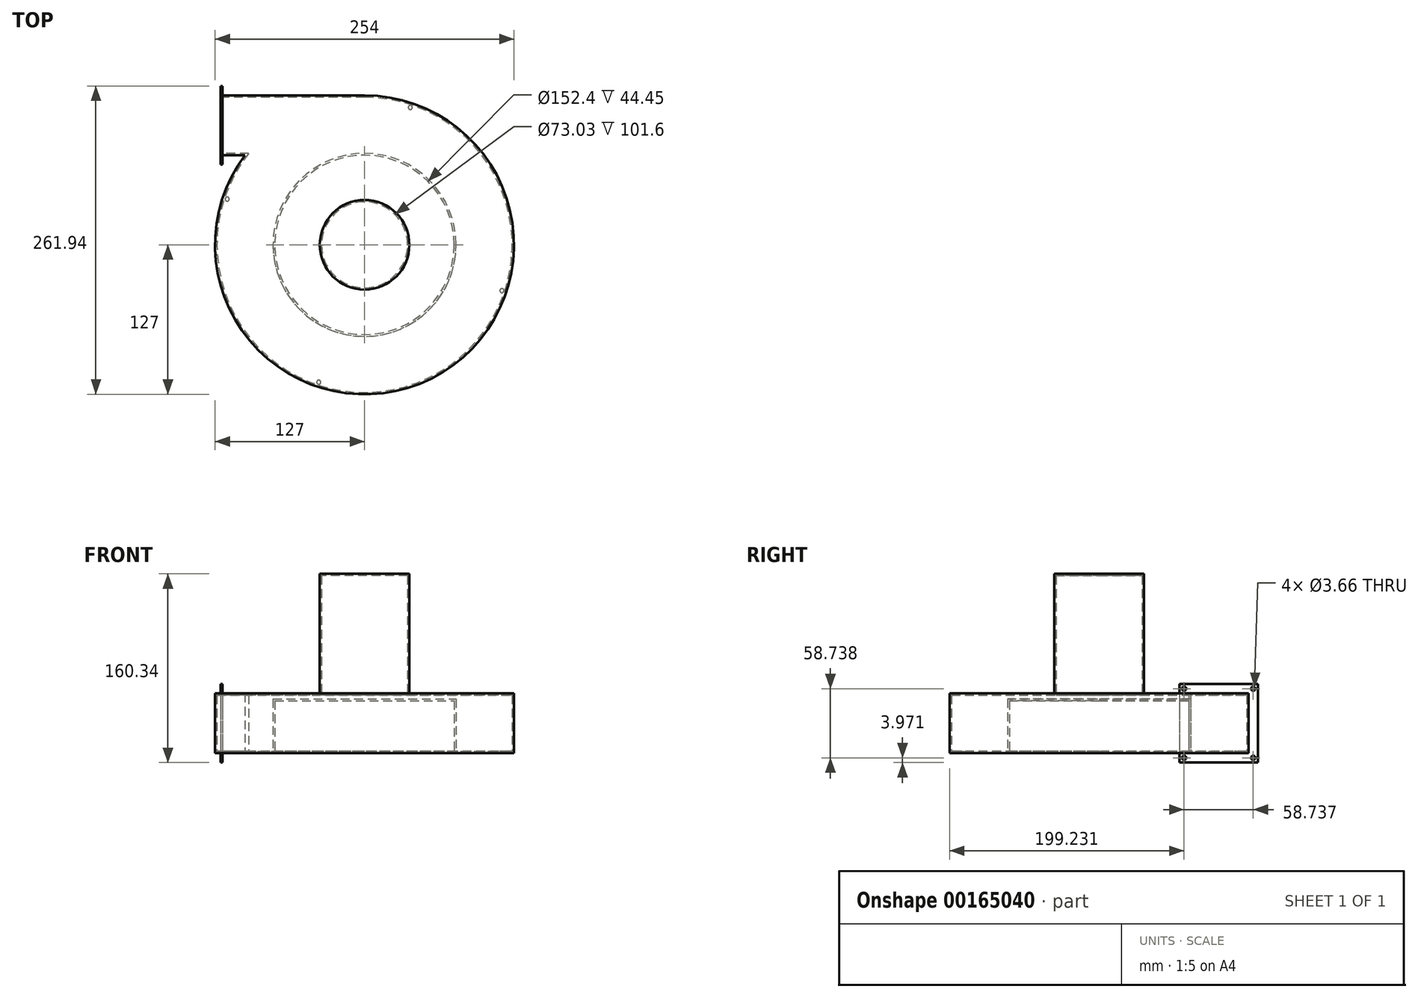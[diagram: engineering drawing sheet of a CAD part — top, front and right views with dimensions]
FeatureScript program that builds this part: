
annotation { "Feature Type Name" : "Feature", "Feature Type Description" : "" }
export const myFeature = defineFeature(function(context is Context, id is Id, definition is map)
    precondition{}
    {
        {
            var Q0;
            Q0=qCreatedBy(makeId("Top.planeOp"),FACE);
            var sketch = newSketch(context, id + "F0", { "sketchPlane" : qUnion([Q0])});
            skLineSegment(sketch, "E0.bottom", {"start": v(-101.6, 76.2) * mm, "end": v(-120.65, 76.2) * mm});
            skLineSegment(sketch, "E0.top", {"start": v(0, 127) * mm, "end": v(-120.65, 127) * mm});
            skLineSegment(sketch, "E1.top", {"start": v(-120.65, 68.26) * mm, "end": v(-122.24, 68.26) * mm});
            skLineSegment(sketch, "E1.left", {"start": v(-120.65, 76.2) * mm, "end": v(-120.65, 68.26) * mm});
            skLineSegment(sketch, "E2.top", {"start": v(-120.65, 134.94) * mm, "end": v(-122.24, 134.94) * mm});
            skLineSegment(sketch, "E2.left", {"start": v(-120.65, 127) * mm, "end": v(-120.65, 134.94) * mm});
            skLineSegment(sketch, "E3", {"start": v(-122.24, 134.94) * mm, "end": v(-122.24, 68.26) * mm});
            skLineSegment(sketch, "E4", {"start": v(-120.65, 76.2) * mm, "end": v(-120.65, 127) * mm, "construction": true});
            skArc(sketch, "E5", {"start": v(-101.6, 76.2) * mm, "mid": v(56.8, -113.6) * mm, "end": v(0, 127) * mm});
            skSolve(sketch);
        }
        {
            var Q0;
            Q0=makeQuery(id+"F0.imprint","IMPRINT",FACE,{"disambiguationData":[TD([[makeQuery(id+"F0.imprint","IMPRINT",EDGE,{"derivedFrom":sQuery(id+"F0.wireOp",EDGE,"E0.bottom")}),-1.0]])]});
            extrude(context, id + "F1", {"entities" : qUnion([Q0]), "depth" : 50.8 * mm});
        }
        {
            var Q0;
            Q0=makeQuery(id+"F1.opExtrude","CAP_FACE",FACE,{"disambiguationData":[OSD([sQuery(id+"F0.wireOp",EDGE,"E0.bottom"),sQuery(id+"F0.wireOp",EDGE,"E0.top"),sQuery(id+"F0.wireOp",EDGE,"E1.top"),sQuery(id+"F0.wireOp",EDGE,"E1.left"),sQuery(id+"F0.wireOp",EDGE,"E2.top"),sQuery(id+"F0.wireOp",EDGE,"E2.left"),sQuery(id+"F0.wireOp",EDGE,"E3"),sQuery(id+"F0.wireOp",EDGE,"E5")])],"isStart":true});
            var sketch = newSketch(context, id + "F2", { "sketchPlane" : qUnion([Q0])});
            skCircle(sketch, "E6", {"center": v(0, 0) * mm, "radius": 76.2 * mm});
            skSolve(sketch);
        }
        {
            var Q0;
            Q0=qSketchRegion(id+"F2",true);
            extrude(context, id + "F3", {"entities" : qUnion([Q0]), "operationType" : NewBodyOperationType.REMOVE, "oppositeDirection" : true, "depth" : 44.45 * mm});
        }
        {
            var Q0;
            Q0=makeQuery(id+"F1.opExtrude","CAP_FACE",FACE,{"disambiguationData":[OSD([sQuery(id+"F0.wireOp",EDGE,"E0.bottom"),sQuery(id+"F0.wireOp",EDGE,"E0.top"),sQuery(id+"F0.wireOp",EDGE,"E1.top"),sQuery(id+"F0.wireOp",EDGE,"E1.left"),sQuery(id+"F0.wireOp",EDGE,"E2.top"),sQuery(id+"F0.wireOp",EDGE,"E2.left"),sQuery(id+"F0.wireOp",EDGE,"E3"),sQuery(id+"F0.wireOp",EDGE,"E5")])],"isStart":false});
            var sketch = newSketch(context, id + "F4", { "sketchPlane" : qUnion([Q0])});
            skCircle(sketch, "E7", {"center": v(0, 0) * mm, "radius": 38.1 * mm});
            skSolve(sketch);
        }
        {
            var Q0;
            Q0=makeQuery(id+"F4.imprint","IMPRINT",FACE,{"disambiguationData":[TD([[makeQuery(id+"F4.imprint","IMPRINT",EDGE,{"derivedFrom":sQuery(id+"F4.wireOp",EDGE,"E7")}),1.0]])]});
            extrude(context, id + "F5", {"entities" : qUnion([Q0]), "operationType" : NewBodyOperationType.ADD, "depth" : 101.6 * mm});
        }
        {
            var Q0;
            Q0=makeQuery(id+"F1.opExtrude","SWEPT_FACE",FACE,{"disambiguationData":[OSD([sQuery(id+"F0.wireOp",EDGE,"E3")])]});
            shell(context, id + "F6", {"entities" : qUnion([Q0]), "thickness" : 1.59 * mm});
        }
        {
            var Q0;
            Q0=makeQuery(id+"F1.opExtrude","SWEPT_FACE",FACE,{"disambiguationData":[OSD([sQuery(id+"F0.wireOp",EDGE,"E3")])]});
            var sketch = newSketch(context, id + "F7", { "sketchPlane" : qUnion([Q0])});
            skLineSegment(sketch, "E8.bottom", {"start": v(-125.41, 49.21) * mm, "end": v(-77.79, 49.21) * mm});
            skLineSegment(sketch, "E8.top", {"start": v(-125.41, 1.59) * mm, "end": v(-77.79, 1.59) * mm});
            skLineSegment(sketch, "E8.left", {"start": v(-125.41, 49.21) * mm, "end": v(-125.41, 1.59) * mm});
            skLineSegment(sketch, "E8.right", {"start": v(-77.79, 49.21) * mm, "end": v(-77.79, 1.59) * mm});
            skPoint(sketch, "E8.middle", {"position": v(-101.6, 25.4) * mm});
            skLineSegment(sketch, "E9.bottom", {"start": v(-68.26, 58.74) * mm, "end": v(-134.94, 58.74) * mm});
            skLineSegment(sketch, "E9.top", {"start": v(-68.26, -7.94) * mm, "end": v(-134.94, -7.94) * mm});
            skLineSegment(sketch, "E9.left", {"start": v(-68.26, 58.74) * mm, "end": v(-68.26, -7.94) * mm});
            skLineSegment(sketch, "E9.right", {"start": v(-134.94, 58.74) * mm, "end": v(-134.94, -7.94) * mm});
            skSolve(sketch);
        }
        {
            var Q0;
            Q0=qSketchRegion(id+"F7",true);
            var Q1;
            Q1=makeQuery(id+"F1.opExtrude","SWEPT_FACE",FACE,{"disambiguationData":[OSD([sQuery(id+"F0.wireOp",EDGE,"E2.left")])]});
            extrude(context, id + "F8", {"entities" : qUnion([Q0]), "operationType" : NewBodyOperationType.ADD, "endBound" : BoundingType.UP_TO_SURFACE, "oppositeDirection" : true, "endBoundEntityFace" : qUnion([Q1]), "depth" : 25.4 * mm});
        }
        {
            var Q0;
            Q0=makeQuery(id+"F1.opExtrude","SWEPT_FACE",FACE,{"disambiguationData":[OSD([sQuery(id+"F0.wireOp",EDGE,"E3")])]});
            var sketch = newSketch(context, id + "F9", { "sketchPlane" : qUnion([Q0])});
            skLineSegment(sketch, "E10", {"start": v(-101.6, 49.21) * mm, "end": v(-101.6, 1.59) * mm, "construction": true});
            skLineSegment(sketch, "E11.bottom", {"start": v(-130.97, 58.74) * mm, "end": v(-134.94, 58.74) * mm, "construction": true});
            skLineSegment(sketch, "E11.top", {"start": v(-130.97, 54.77) * mm, "end": v(-134.94, 54.77) * mm, "construction": true});
            skLineSegment(sketch, "E11.left", {"start": v(-130.97, 58.74) * mm, "end": v(-130.97, 54.77) * mm, "construction": true});
            skLineSegment(sketch, "E11.right", {"start": v(-134.94, 58.74) * mm, "end": v(-134.94, 54.77) * mm, "construction": true});
            skLineSegment(sketch, "E12.bottom", {"start": v(-130.97, 54.77) * mm, "end": v(-72.23, 54.77) * mm, "construction": true});
            skLineSegment(sketch, "E12.top", {"start": v(-130.97, -3.97) * mm, "end": v(-72.23, -3.97) * mm, "construction": true});
            skLineSegment(sketch, "E12.left", {"start": v(-130.97, 54.77) * mm, "end": v(-130.97, -3.97) * mm, "construction": true});
            skLineSegment(sketch, "E12.right", {"start": v(-72.23, 54.77) * mm, "end": v(-72.23, -3.97) * mm, "construction": true});
            skPoint(sketch, "E12.middle", {"position": v(-101.6, 25.4) * mm});
            skCircle(sketch, "E13", {"center": v(-130.97, 54.77) * mm, "radius": 1.83 * mm});
            skCircle(sketch, "E14", {"center": v(-72.23, 54.77) * mm, "radius": 1.83 * mm});
            skCircle(sketch, "E15", {"center": v(-72.23, -3.97) * mm, "radius": 1.83 * mm});
            skCircle(sketch, "E16", {"center": v(-130.97, -3.97) * mm, "radius": 1.83 * mm});
            skSolve(sketch);
        }
        {
            var Q0;
            Q0=qSketchRegion(id+"F9",true);
            var Q1;
            Q1=makeQuery(id+"F1.opExtrude","SWEPT_FACE",FACE,{"disambiguationData":[OSD([sQuery(id+"F0.wireOp",EDGE,"E2.left")])]});
            extrude(context, id + "F10", {"entities" : qUnion([Q0]), "operationType" : NewBodyOperationType.REMOVE, "endBound" : BoundingType.UP_TO_SURFACE, "oppositeDirection" : true, "endBoundEntityFace" : qUnion([Q1]), "depth" : 25.4 * mm});
        }
        {
            var Q0;
            Q0=makeQuery(id+"F1.opExtrude","CAP_FACE",FACE,{"disambiguationData":[OSD([sQuery(id+"F0.wireOp",EDGE,"E0.bottom"),sQuery(id+"F0.wireOp",EDGE,"E0.top"),sQuery(id+"F0.wireOp",EDGE,"E1.top"),sQuery(id+"F0.wireOp",EDGE,"E1.left"),sQuery(id+"F0.wireOp",EDGE,"E2.top"),sQuery(id+"F0.wireOp",EDGE,"E2.left"),sQuery(id+"F0.wireOp",EDGE,"E3"),sQuery(id+"F0.wireOp",EDGE,"E5")])],"isStart":true});
            var sketch = newSketch(context, id + "F11", { "sketchPlane" : qUnion([Q0])});
            skLineSegment(sketch, "E17.bottom", {"start": v(-116.72, -38.9) * mm, "end": v(-38.9, 116.72) * mm, "construction": true});
            skLineSegment(sketch, "E17.top", {"start": v(38.9, -116.72) * mm, "end": v(116.72, 38.9) * mm, "construction": true});
            skLineSegment(sketch, "E17.left", {"start": v(-116.72, -38.9) * mm, "end": v(38.9, -116.72) * mm, "construction": true});
            skLineSegment(sketch, "E17.right", {"start": v(-38.9, 116.72) * mm, "end": v(116.72, 38.9) * mm, "construction": true});
            skPoint(sketch, "E17.middle", {"position": v(0, 0) * mm});
            skCircle(sketch, "E18", {"center": v(-38.9, 116.72) * mm, "radius": 3.97 * mm, "construction": true});
            skArc(sketch, "E19", {"start": v(-101.6, -76.2) * mm, "mid": v(-56.8, -113.6) * mm, "end": v(0, -127) * mm, "construction": true});
            skLineSegment(sketch, "E20", {"start": v(0, 0) * mm, "end": v(-38.9, -77.81) * mm, "construction": true});
            skLineSegment(sketch, "E21", {"start": v(-38.9, -77.81) * mm, "end": v(-56.8, -113.6) * mm, "construction": true});
            skCircle(sketch, "E22", {"center": v(38.9, -116.72) * mm, "radius": 1.73 * mm});
            skCircle(sketch, "E23", {"center": v(-116.72, -38.9) * mm, "radius": 1.73 * mm});
            skCircle(sketch, "E24", {"center": v(-38.9, 116.72) * mm, "radius": 1.73 * mm});
            skCircle(sketch, "E25", {"center": v(116.72, 38.9) * mm, "radius": 1.73 * mm});
            skSolve(sketch);
        }
        {
            var Q0;
            Q0=qSketchRegion(id+"F11",true);
            extrude(context, id + "F12", {"entities" : qUnion([Q0]), "operationType" : NewBodyOperationType.REMOVE, "oppositeDirection" : true, "depth" : 12.7 * mm});
        }
    });
